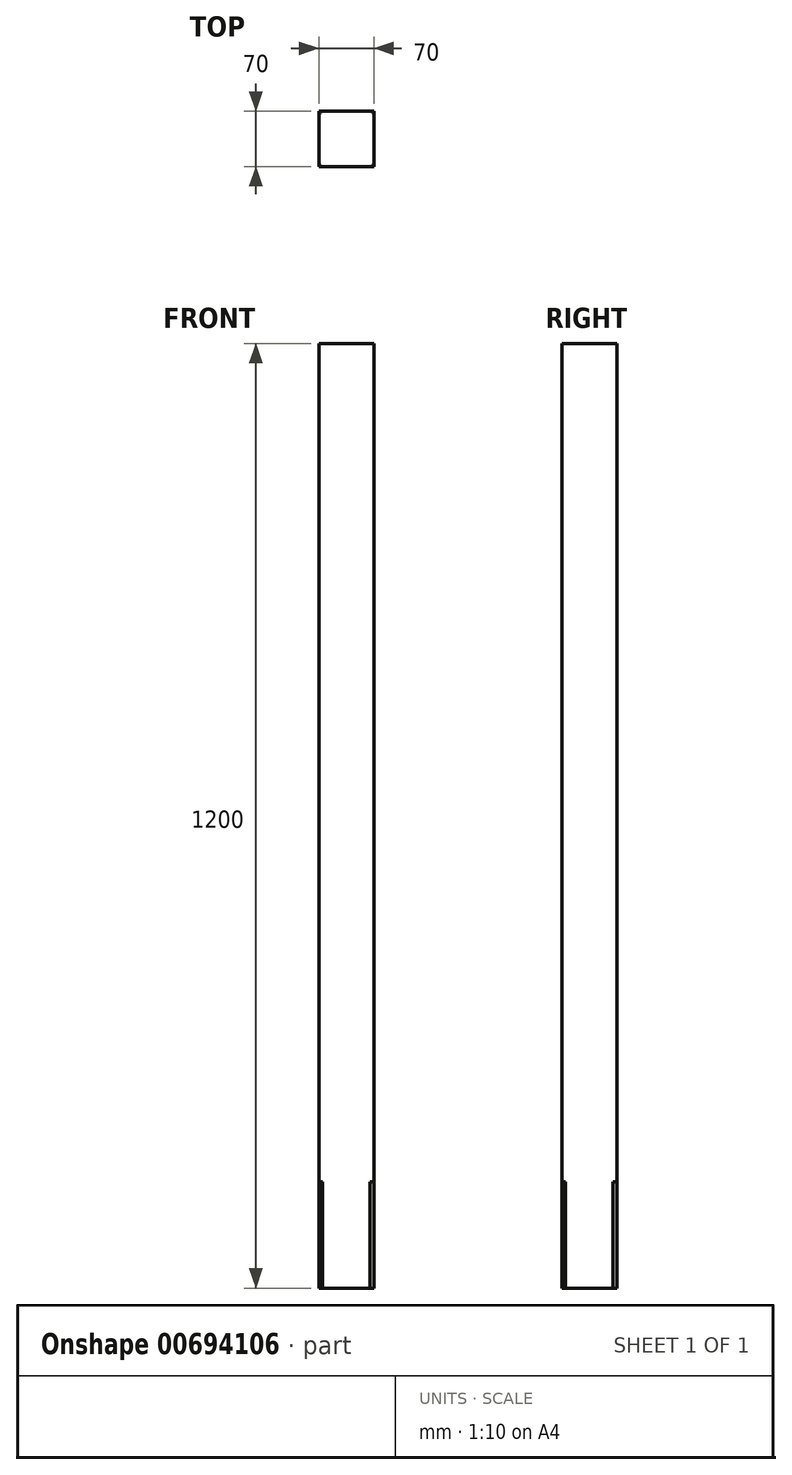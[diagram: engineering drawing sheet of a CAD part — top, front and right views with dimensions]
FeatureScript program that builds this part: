
annotation { "Feature Type Name" : "Feature", "Feature Type Description" : "" }
export const myFeature = defineFeature(function(context is Context, id is Id, definition is map)
    precondition{}
    {
        {
            var Q0;
            Q0=qCreatedBy(makeId("Top.planeOp"),FACE);
            var sketch = newSketch(context, id + "F0", { "sketchPlane" : qUnion([Q0])});
            skLineSegment(sketch, "E0.bottom", {"start": v(-35, -35) * mm, "end": v(35, -35) * mm});
            skLineSegment(sketch, "E0.top", {"start": v(-35, 35) * mm, "end": v(35, 35) * mm});
            skLineSegment(sketch, "E0.left", {"start": v(-35, -35) * mm, "end": v(-35, 35) * mm});
            skLineSegment(sketch, "E0.right", {"start": v(35, -35) * mm, "end": v(35, 35) * mm});
            skSolve(sketch);
        }
        {
            var Q0;
            Q0=makeQuery(id+"F0.imprint","IMPRINT",FACE,{"disambiguationData":[TD([[makeQuery(id+"F0.imprint","IMPRINT",EDGE,{"derivedFrom":sQuery(id+"F0.wireOp",EDGE,"E0.bottom")}),1.0]])]});
            extrude(context, id + "F1", {"entities" : qUnion([Q0]), "depth" : (150 - 15) * mm, "offsetDistance" : 25 * mm});
        }
        {
            var Q0;
            Q0=makeQuery(id+"F1.opExtrude","SWEPT_EDGE",EDGE,{"disambiguationData":[OSD([sQuery(id+"F0.wireOp",EDGE,"E0.bottom"),sQuery(id+"F0.wireOp",EDGE,"E0.right")])]});
            var Q1;
            Q1=makeQuery(id+"F1.opExtrude","SWEPT_EDGE",EDGE,{"disambiguationData":[OSD([sQuery(id+"F0.wireOp",EDGE,"E0.bottom"),sQuery(id+"F0.wireOp",EDGE,"E0.left")])]});
            var Q2;
            Q2=makeQuery(id+"F1.opExtrude","SWEPT_EDGE",EDGE,{"disambiguationData":[OSD([sQuery(id+"F0.wireOp",EDGE,"E0.top"),sQuery(id+"F0.wireOp",EDGE,"E0.right")])]});
            var Q3;
            Q3=makeQuery(id+"F1.opExtrude","SWEPT_EDGE",EDGE,{"disambiguationData":[OSD([sQuery(id+"F0.wireOp",EDGE,"E0.top"),sQuery(id+"F0.wireOp",EDGE,"E0.left")])]});
            chamfer(context, id + "F2", {"entities" : qUnion([Q0, Q1, Q2, Q3]), "width" : 5 * mm, "tangentPropagation" : true});
        }
        {
            var Q0;
            Q0=makeQuery(id+"F1.opExtrude","CAP_FACE",FACE,{"disambiguationData":[OSD([sQuery(id+"F0.wireOp",EDGE,"E0.bottom"),sQuery(id+"F0.wireOp",EDGE,"E0.top"),sQuery(id+"F0.wireOp",EDGE,"E0.left"),sQuery(id+"F0.wireOp",EDGE,"E0.right")])],"isStart":false});
            var sketch = newSketch(context, id + "F3", { "sketchPlane" : qUnion([Q0])});
            skLineSegment(sketch, "E1.bottom", {"start": v(-35, 35) * mm, "end": v(35, 35) * mm});
            skLineSegment(sketch, "E1.top", {"start": v(-35, -35) * mm, "end": v(35, -35) * mm});
            skLineSegment(sketch, "E1.left", {"start": v(-35, 35) * mm, "end": v(-35, -35) * mm});
            skLineSegment(sketch, "E1.right", {"start": v(35, 35) * mm, "end": v(35, -35) * mm});
            skSolve(sketch);
        }
        {
            var Q0;
            Q0 = qSketchRegion(id + "F3", true);
            extrude(context, id + "F4", {"entities" : qUnion([Q0]), "operationType" : NewBodyOperationType.ADD, "depth" : (1200 - 150 + 15) * mm, "offsetDistance" : 25 * mm});
        }
    });
